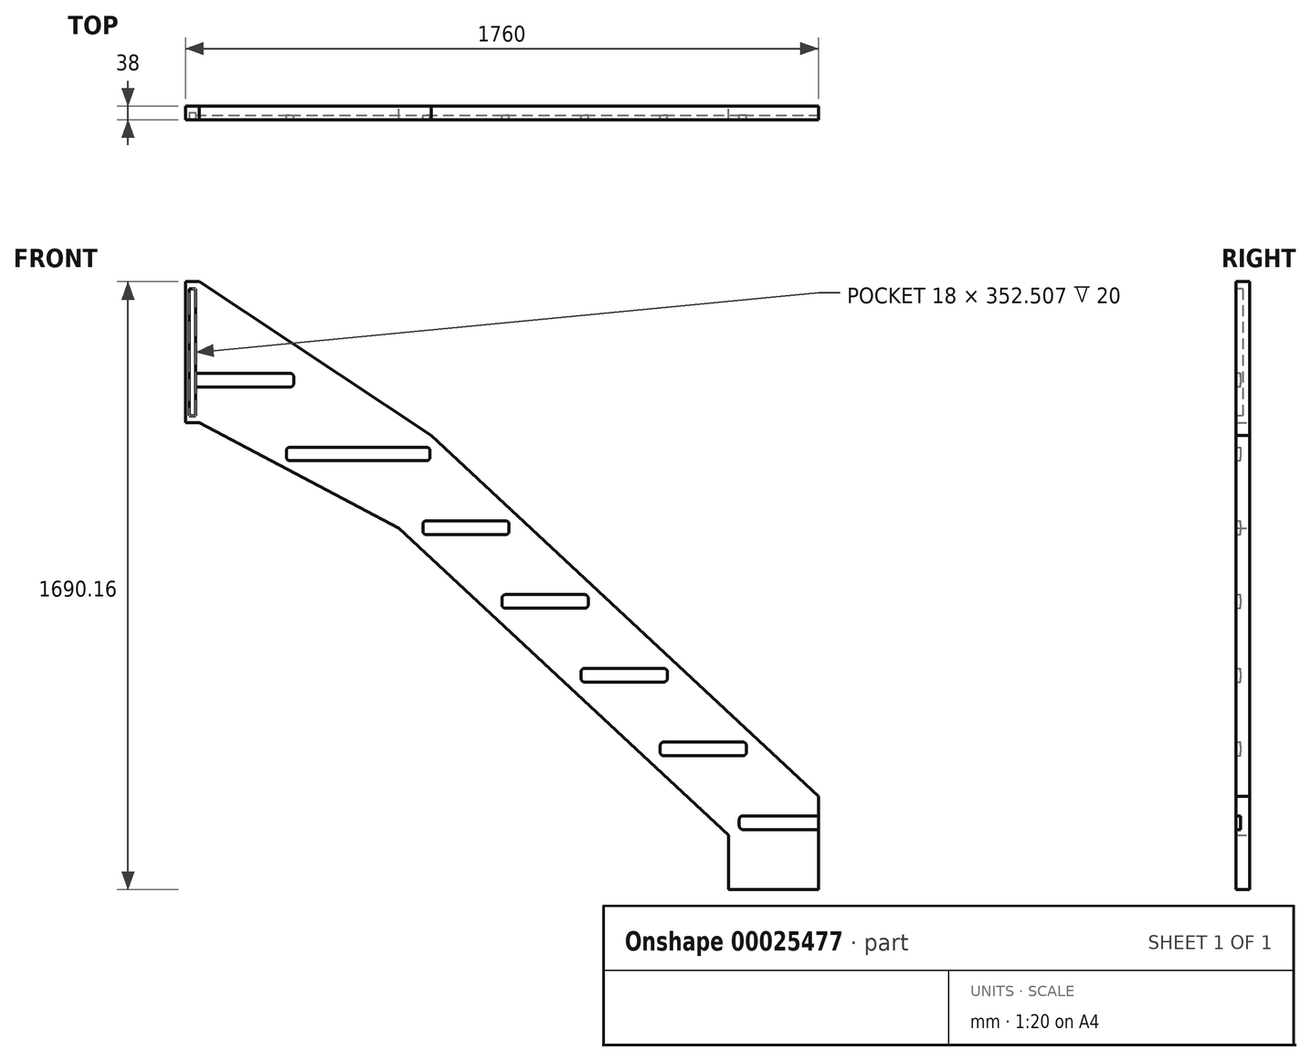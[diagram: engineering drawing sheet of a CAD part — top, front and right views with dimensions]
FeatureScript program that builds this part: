
annotation { "Feature Type Name" : "Feature", "Feature Type Description" : "" }
export const myFeature = defineFeature(function(context is Context, id is Id, definition is map)
    precondition{}
    {
        {
            var Q0;
            Q0=qCreatedBy(makeId("Front.planeOp"),FACE);
            var sketch = newSketch(context, id + "F0", { "sketchPlane" : qUnion([Q0])});
            skLineSegment(sketch, "E0", {"start": v(-854.2, 590.2) * mm, "end": v(-589.2, 590.2) * mm});
            skLineSegment(sketch, "E1", {"start": v(670, -640.08) * mm, "end": v(880, -640.08) * mm});
            skLineSegment(sketch, "E2", {"start": v(670, -678.08) * mm, "end": v(880, -678.08) * mm});
            skLineSegment(sketch, "E3", {"start": v(880, -845.08) * mm, "end": v(880, -585.41) * mm});
            skLineSegment(sketch, "E4", {"start": v(630, -845.08) * mm, "end": v(630, -694.17) * mm});
            skLineSegment(sketch, "E5", {"start": v(880, -585.41) * mm, "end": v(-196.64, 417.82) * mm});
            skLineSegment(sketch, "E6", {"start": v(630, -694.17) * mm, "end": v(-286.86, 160.18) * mm});
            skLineSegment(sketch, "E7", {"start": v(450, -435.08) * mm, "end": v(670, -435.08) * mm});
            skLineSegment(sketch, "E8", {"start": v(450, -473.08) * mm, "end": v(670, -473.08) * mm});
            skArc(sketch, "E9", {"start": v(670, -473.08) * mm, "mid": v(677.07, -470.16) * mm, "end": v(680, -463.08) * mm});
            skLineSegment(sketch, "E10", {"start": v(680, -445.08) * mm, "end": v(680, -463.08) * mm});
            skArc(sketch, "E11", {"start": v(680, -445.08) * mm, "mid": v(677.07, -438.01) * mm, "end": v(670, -435.08) * mm});
            skLineSegment(sketch, "E12", {"start": v(230, -230.08) * mm, "end": v(450, -230.08) * mm});
            skLineSegment(sketch, "E13", {"start": v(230, -268.08) * mm, "end": v(450, -268.08) * mm});
            skArc(sketch, "E14", {"start": v(450, -268.08) * mm, "mid": v(457.07, -265.16) * mm, "end": v(460, -258.08) * mm});
            skLineSegment(sketch, "E15", {"start": v(460, -240.08) * mm, "end": v(460, -258.08) * mm});
            skArc(sketch, "E16", {"start": v(460, -240.08) * mm, "mid": v(457.07, -233.01) * mm, "end": v(450, -230.08) * mm});
            skLineSegment(sketch, "E17", {"start": v(10, -25.08) * mm, "end": v(230, -25.08) * mm});
            skLineSegment(sketch, "E18", {"start": v(10, -63.08) * mm, "end": v(230, -63.08) * mm});
            skArc(sketch, "E19", {"start": v(230, -63.08) * mm, "mid": v(237.07, -60.16) * mm, "end": v(240, -53.08) * mm});
            skLineSegment(sketch, "E20", {"start": v(240, -35.08) * mm, "end": v(240, -53.08) * mm});
            skArc(sketch, "E21", {"start": v(240, -35.08) * mm, "mid": v(237.07, -28.01) * mm, "end": v(230, -25.08) * mm});
            skLineSegment(sketch, "E22", {"start": v(-210, 179.92) * mm, "end": v(10, 179.92) * mm});
            skLineSegment(sketch, "E23", {"start": v(-210, 141.92) * mm, "end": v(10, 141.92) * mm});
            skArc(sketch, "E24", {"start": v(10, 141.92) * mm, "mid": v(17.07, 144.84) * mm, "end": v(20, 151.92) * mm});
            skLineSegment(sketch, "E25", {"start": v(20, 169.92) * mm, "end": v(20, 151.92) * mm});
            skArc(sketch, "E26", {"start": v(20, 169.92) * mm, "mid": v(17.07, 176.99) * mm, "end": v(10, 179.92) * mm});
            skLineSegment(sketch, "E27", {"start": v(-220, 169.92) * mm, "end": v(-220, 151.92) * mm});
            skLineSegment(sketch, "E28", {"start": v(0, -35.08) * mm, "end": v(0, -53.08) * mm});
            skLineSegment(sketch, "E29", {"start": v(220, -240.08) * mm, "end": v(220, -258.08) * mm});
            skLineSegment(sketch, "E30", {"start": v(440, -445.08) * mm, "end": v(440, -463.08) * mm});
            skLineSegment(sketch, "E31", {"start": v(660, -650.08) * mm, "end": v(660, -668.08) * mm});
            skLineSegment(sketch, "E32", {"start": v(-854.2, 551.92) * mm, "end": v(-589.2, 551.92) * mm});
            skLineSegment(sketch, "E33", {"start": v(-286.86, 160.18) * mm, "end": v(-842, 452.58) * mm});
            skLineSegment(sketch, "E34", {"start": v(-880, 845.08) * mm, "end": v(-880, 452.58) * mm});
            skLineSegment(sketch, "E35", {"start": v(-880, 845.08) * mm, "end": v(-842, 845.08) * mm});
            skLineSegment(sketch, "E36", {"start": v(-842, 845.08) * mm, "end": v(-196.64, 417.82) * mm});
            skLineSegment(sketch, "E37", {"start": v(-842, 452.58) * mm, "end": v(-880, 452.58) * mm});
            skArc(sketch, "E38", {"start": v(-210, 179.92) * mm, "mid": v(-217.07, 176.99) * mm, "end": v(-220, 169.92) * mm});
            skArc(sketch, "E39", {"start": v(-220, 151.92) * mm, "mid": v(-217.07, 144.84) * mm, "end": v(-210, 141.92) * mm});
            skArc(sketch, "E40", {"start": v(10, -25.08) * mm, "mid": v(2.93, -28.01) * mm, "end": v(0, -35.08) * mm});
            skArc(sketch, "E41", {"start": v(0, -53.08) * mm, "mid": v(2.93, -60.16) * mm, "end": v(10, -63.08) * mm});
            skArc(sketch, "E42", {"start": v(230, -230.08) * mm, "mid": v(222.93, -233.01) * mm, "end": v(220, -240.08) * mm});
            skArc(sketch, "E43", {"start": v(220, -258.08) * mm, "mid": v(222.93, -265.16) * mm, "end": v(230, -268.08) * mm});
            skArc(sketch, "E44", {"start": v(450, -435.08) * mm, "mid": v(442.93, -438.01) * mm, "end": v(440, -445.08) * mm});
            skArc(sketch, "E45", {"start": v(440, -463.08) * mm, "mid": v(442.93, -470.16) * mm, "end": v(450, -473.08) * mm});
            skArc(sketch, "E46", {"start": v(670, -640.08) * mm, "mid": v(662.93, -643.01) * mm, "end": v(660, -650.08) * mm});
            skArc(sketch, "E47", {"start": v(660, -668.08) * mm, "mid": v(662.93, -675.16) * mm, "end": v(670, -678.08) * mm});
            skArc(sketch, "E48", {"start": v(-589.2, 384.92) * mm, "mid": v(-596.28, 381.99) * mm, "end": v(-599.2, 374.92) * mm});
            skArc(sketch, "E49", {"start": v(-599.2, 356.92) * mm, "mid": v(-596.28, 349.84) * mm, "end": v(-589.2, 346.92) * mm});
            skLineSegment(sketch, "E50", {"start": v(880, -845.08) * mm, "end": v(630, -845.08) * mm});
            skLineSegment(sketch, "E51", {"start": v(-599.2, 374.92) * mm, "end": v(-599.2, 356.92) * mm});
            skLineSegment(sketch, "E52", {"start": v(-589.2, 346.92) * mm, "end": v(-210, 346.92) * mm});
            skLineSegment(sketch, "E53", {"start": v(-589.2, 384.92) * mm, "end": v(-210, 384.92) * mm});
            skLineSegment(sketch, "E54", {"start": v(-200, 374.92) * mm, "end": v(-200, 356.92) * mm});
            skPoint(sketch, "E55.visualSharp", {"position": v(-200, 384.92) * mm});
            skArc(sketch, "E55.filletArc", {"start": v(-200, 374.92) * mm, "mid": v(-202.93, 381.99) * mm, "end": v(-210, 384.92) * mm});
            skPoint(sketch, "E56.visualSharp", {"position": v(-200, 346.92) * mm});
            skArc(sketch, "E56.filletArc", {"start": v(-210, 346.92) * mm, "mid": v(-202.93, 349.84) * mm, "end": v(-200, 356.92) * mm});
            skLineSegment(sketch, "E57", {"start": v(-854.2, 590.2) * mm, "end": v(-854.2, 551.92) * mm});
            skLineSegment(sketch, "E58", {"start": v(-579.2, 580.2) * mm, "end": v(-579.2, 561.92) * mm});
            skPoint(sketch, "E59.visualSharp", {"position": v(-579.2, 590.2) * mm});
            skArc(sketch, "E59.filletArc", {"start": v(-579.2, 580.2) * mm, "mid": v(-582.13, 587.27) * mm, "end": v(-589.2, 590.2) * mm});
            skPoint(sketch, "E60.visualSharp", {"position": v(-579.2, 551.92) * mm});
            skArc(sketch, "E60.filletArc", {"start": v(-589.2, 551.92) * mm, "mid": v(-582.13, 554.84) * mm, "end": v(-579.2, 561.92) * mm});
            skSolve(sketch);
        }
        {
            var Q0;
            Q0=makeQuery(id+"F0.imprint","IMPRINT",FACE,{"disambiguationData":[TD([[makeQuery(id+"F0.imprint","IMPRINT",EDGE,{"derivedFrom":sQuery(id+"F0.wireOp",EDGE,"E0")}),1.0]])]});
            extrude(context, id + "F1", {"entities" : qUnion([Q0]), "depth" : 38 * mm});
        }
        {
            var Q0;
            Q0=makeQuery(id+"F0.imprint","IMPRINT",FACE,{"disambiguationData":[TD([[makeQuery(id+"F0.imprint","IMPRINT",EDGE,{"derivedFrom":sQuery(id+"F0.wireOp",EDGE,"E0")}),-1.0]])]});
            extrude(context, id + "F2", {"entities" : qUnion([Q0]), "operationType" : NewBodyOperationType.ADD, "depth" : 25.5 * mm});
        }
        {
            var Q0;
            Q0=makeQuery(id+"F0.imprint","IMPRINT",FACE,{"disambiguationData":[TD([[makeQuery(id+"F0.imprint","IMPRINT",EDGE,{"derivedFrom":sQuery(id+"F0.wireOp",EDGE,"107d2413-fdc3-4c5c-9f5b-b8e41b567185")}),-1.0]])]});
            var Q1;
            Q1=makeQuery(id+"F0.imprint","IMPRINT",FACE,{"disambiguationData":[TD([[makeQuery(id+"F0.imprint","IMPRINT",EDGE,{"derivedFrom":sQuery(id+"F0.wireOp",EDGE,"E22")}),-1.0]])]});
            var Q2;
            Q2=makeQuery(id+"F0.imprint","IMPRINT",FACE,{"disambiguationData":[TD([[makeQuery(id+"F0.imprint","IMPRINT",EDGE,{"derivedFrom":sQuery(id+"F0.wireOp",EDGE,"E17")}),-1.0]])]});
            var Q3;
            Q3=makeQuery(id+"F0.imprint","IMPRINT",FACE,{"disambiguationData":[TD([[makeQuery(id+"F0.imprint","IMPRINT",EDGE,{"derivedFrom":sQuery(id+"F0.wireOp",EDGE,"E12")}),-1.0]])]});
            var Q4;
            Q4=makeQuery(id+"F0.imprint","IMPRINT",FACE,{"disambiguationData":[TD([[makeQuery(id+"F0.imprint","IMPRINT",EDGE,{"derivedFrom":sQuery(id+"F0.wireOp",EDGE,"E7")}),-1.0]])]});
            var Q5;
            {var subQ2=sQuery(id+"F0.wireOp",EDGE,"E1");Q5=makeQuery(id+"F0.imprint","IMPRINT",FACE,{"disambiguationData":[TD([[makeQuery(id+"F0.imprint","IMPRINT",EDGE,{"derivedFrom":subQ2}),-1.0]])]});}
            extrude(context, id + "F3", {"entities" : qUnion([Q0, Q1, Q2, Q3, Q4, Q5]), "operationType" : NewBodyOperationType.ADD, "depth" : 25.5 * mm});
        }
        {
            var Q0;
            Q0=makeQuery(id+"F0.imprint","IMPRINT",FACE,{"disambiguationData":[TD([[makeQuery(id+"F0.imprint","IMPRINT",EDGE,{"derivedFrom":sQuery(id+"F0.wireOp",EDGE,"E48")}),1.0]])]});
            extrude(context, id + "F4", {"entities" : qUnion([Q0]), "operationType" : NewBodyOperationType.ADD, "depth" : 25 * mm});
        }
        {
            var Q0;
            Q0=makeQuery(id+"F0.imprint","IMPRINT",FACE,{"disambiguationData":[TD([[makeQuery(id+"F0.imprint","IMPRINT",EDGE,{"derivedFrom":sQuery(id+"F0.wireOp",EDGE,"E48")}),1.0]])]});
            extrude(context, id + "F5", {"entities" : qUnion([Q0]), "operationType" : NewBodyOperationType.ADD, "depth" : 25.5 * mm});
        }
        {
            var Q0;
            Q0=makeQuery(id+"F1.opExtrude","CAP_FACE",FACE,{"disambiguationData":[OSD([sQuery(id+"F0.wireOp",EDGE,"E0"),sQuery(id+"F0.wireOp",EDGE,"E1"),sQuery(id+"F0.wireOp",EDGE,"E2"),sQuery(id+"F0.wireOp",EDGE,"E3"),sQuery(id+"F0.wireOp",EDGE,"E4"),sQuery(id+"F0.wireOp",EDGE,"E5"),sQuery(id+"F0.wireOp",EDGE,"E6"),sQuery(id+"F0.wireOp",EDGE,"E7"),sQuery(id+"F0.wireOp",EDGE,"E8"),sQuery(id+"F0.wireOp",EDGE,"E9"),sQuery(id+"F0.wireOp",EDGE,"E10"),sQuery(id+"F0.wireOp",EDGE,"E11"),sQuery(id+"F0.wireOp",EDGE,"E12"),sQuery(id+"F0.wireOp",EDGE,"E13"),sQuery(id+"F0.wireOp",EDGE,"E14"),sQuery(id+"F0.wireOp",EDGE,"E15"),sQuery(id+"F0.wireOp",EDGE,"E16"),sQuery(id+"F0.wireOp",EDGE,"E17"),sQuery(id+"F0.wireOp",EDGE,"E18"),sQuery(id+"F0.wireOp",EDGE,"E19"),sQuery(id+"F0.wireOp",EDGE,"E20"),sQuery(id+"F0.wireOp",EDGE,"E21"),sQuery(id+"F0.wireOp",EDGE,"E22"),sQuery(id+"F0.wireOp",EDGE,"E23"),sQuery(id+"F0.wireOp",EDGE,"E24"),sQuery(id+"F0.wireOp",EDGE,"E25"),sQuery(id+"F0.wireOp",EDGE,"E26"),sQuery(id+"F0.wireOp",EDGE,"E27"),sQuery(id+"F0.wireOp",EDGE,"E28"),sQuery(id+"F0.wireOp",EDGE,"E29"),sQuery(id+"F0.wireOp",EDGE,"E30"),sQuery(id+"F0.wireOp",EDGE,"E31"),sQuery(id+"F0.wireOp",EDGE,"E32"),sQuery(id+"F0.wireOp",EDGE,"E33"),sQuery(id+"F0.wireOp",EDGE,"E34"),sQuery(id+"F0.wireOp",EDGE,"E35"),sQuery(id+"F0.wireOp",EDGE,"E36"),sQuery(id+"F0.wireOp",EDGE,"E37"),sQuery(id+"F0.wireOp",EDGE,"E38"),sQuery(id+"F0.wireOp",EDGE,"E39"),sQuery(id+"F0.wireOp",EDGE,"E40"),sQuery(id+"F0.wireOp",EDGE,"E41"),sQuery(id+"F0.wireOp",EDGE,"E42"),sQuery(id+"F0.wireOp",EDGE,"E43"),sQuery(id+"F0.wireOp",EDGE,"E44"),sQuery(id+"F0.wireOp",EDGE,"E45"),sQuery(id+"F0.wireOp",EDGE,"E46"),sQuery(id+"F0.wireOp",EDGE,"E47"),sQuery(id+"F0.wireOp",EDGE,"E48"),sQuery(id+"F0.wireOp",EDGE,"E49"),sQuery(id+"F0.wireOp",EDGE,"E50"),sQuery(id+"F0.wireOp",EDGE,"E51"),sQuery(id+"F0.wireOp",EDGE,"E52"),sQuery(id+"F0.wireOp",EDGE,"E53"),sQuery(id+"F0.wireOp",EDGE,"E54"),sQuery(id+"F0.wireOp",EDGE,"E55.filletArc"),sQuery(id+"F0.wireOp",EDGE,"E56.filletArc"),sQuery(id+"F0.wireOp",EDGE,"E57"),sQuery(id+"F0.wireOp",EDGE,"E58"),sQuery(id+"F0.wireOp",EDGE,"E59.filletArc"),sQuery(id+"F0.wireOp",EDGE,"E60.filletArc")])],"isStart":false});
            var sketch = newSketch(context, id + "F6", { "sketchPlane" : qUnion([Q0])});
            skLineSegment(sketch, "E61.bottom", {"start": v(-870, 825.08) * mm, "end": v(-852, 825.08) * mm});
            skLineSegment(sketch, "E61.top", {"start": v(-870, 472.58) * mm, "end": v(-852, 472.58) * mm});
            skLineSegment(sketch, "E61.left", {"start": v(-870, 825.08) * mm, "end": v(-870, 472.58) * mm});
            skLineSegment(sketch, "E61.right", {"start": v(-852, 825.08) * mm, "end": v(-852, 472.58) * mm});
            skSolve(sketch);
        }
        {
            var Q0;
            Q0=makeQuery(id+"F6.imprint","IMPRINT",FACE,{"disambiguationData":[TD([[makeQuery(id+"F6.imprint","IMPRINT",EDGE,{"derivedFrom":sQuery(id+"F6.wireOp",EDGE,"E61.bottom")}),-1.0]])]});
            extrude(context, id + "F7", {"entities" : qUnion([Q0]), "operationType" : NewBodyOperationType.ADD, "oppositeDirection" : true, "depth" : 20 * mm});
        }
        {
            var Q0;
            Q0 = qSketchRegion(id + "F6", true);
            extrude(context, id + "F8", {"entities" : qUnion([Q0]), "operationType" : NewBodyOperationType.REMOVE, "oppositeDirection" : true, "depth" : 20 * mm});
        }
        {
            var Q0;
            Q0=sQuery(id+"F0.wireOp",EDGE,"E6");
            var Q1;
            Q1=sQuery(id+"F0.wireOp",EDGE,"E33");
            var Q2;
            Q2=sQuery(id+"F0.wireOp",EDGE,"E4");
            var Q3;
            Q3=sQuery(id+"F0.wireOp",EDGE,"E50");
            var Q4;
            Q4=sQuery(id+"F0.wireOp",EDGE,"E3");
            var Q5;
            Q5=sQuery(id+"F0.wireOp",EDGE,"E5");
            var Q6;
            Q6=sQuery(id+"F0.wireOp",EDGE,"E36");
            var Q7;
            Q7=sQuery(id+"F0.wireOp",EDGE,"E35");
            var Q8;
            Q8=sQuery(id+"F0.wireOp",EDGE,"E34");
            var Q9;
            Q9=sQuery(id+"F0.wireOp",EDGE,"E37");
            extrude(context, id + "F9", {"bodyType" : ToolBodyType.SURFACE, "surfaceEntities" : qUnion([Q0, Q1, Q2, Q3, Q4, Q5, Q6, Q7, Q8, Q9]), "depth" : 38 * mm});
        }
    });
